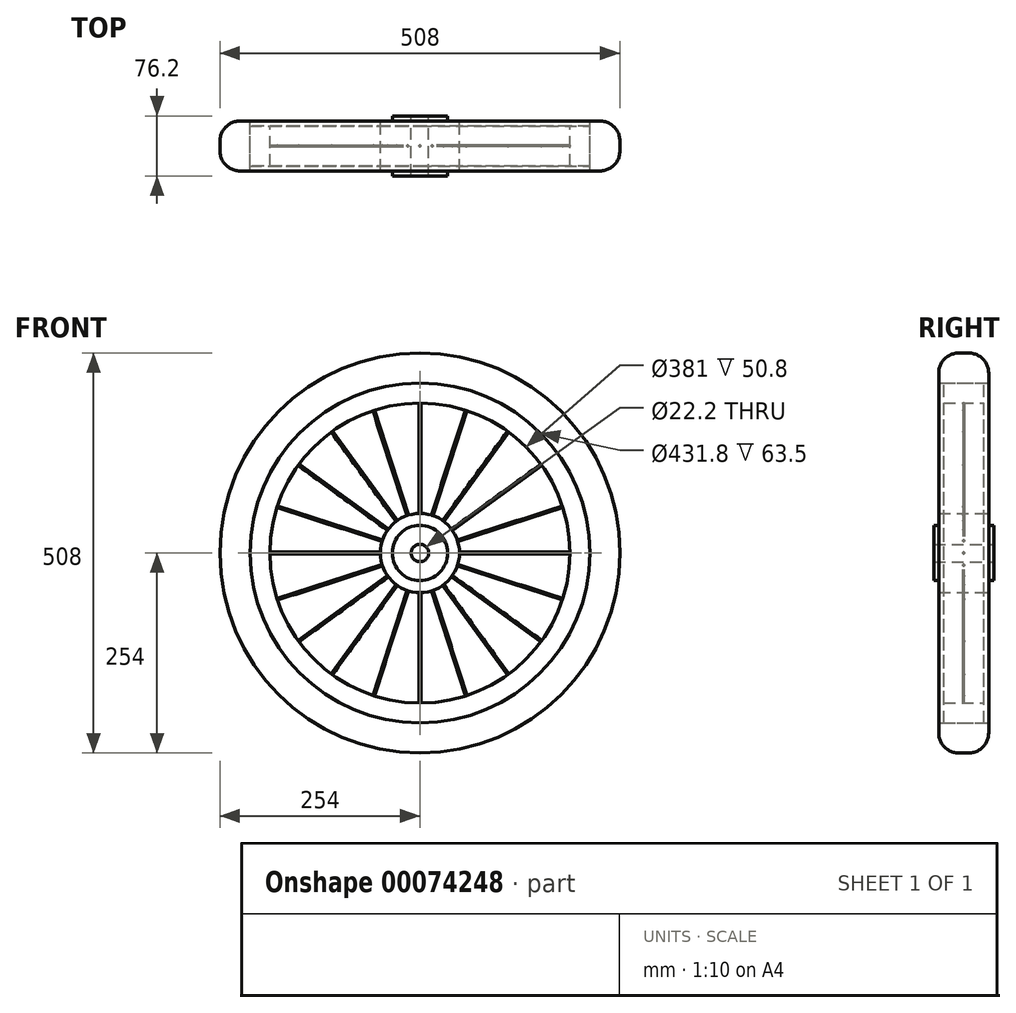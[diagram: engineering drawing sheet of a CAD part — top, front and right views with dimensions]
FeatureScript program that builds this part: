
annotation { "Feature Type Name" : "Feature", "Feature Type Description" : "" }
export const myFeature = defineFeature(function(context is Context, id is Id, definition is map)
    precondition{}
    {
        {
            var Q0;
            Q0=qCreatedBy(makeId("Front.planeOp"),FACE);
            var sketch = newSketch(context, id + "F0", { "sketchPlane" : qUnion([Q0])});
            skCircle(sketch, "E0", {"center": v(0, 0) * mm, "radius": 11.1 * mm});
            skCircle(sketch, "E1", {"center": v(0, 0) * mm, "radius": 35.13 * mm});
            skCircle(sketch, "E2", {"center": v(0, 0) * mm, "radius": 50.24 * mm});
            skCircle(sketch, "E3", {"center": v(0, 0) * mm, "radius": 190.5 * mm});
            skCircle(sketch, "E4", {"center": v(0, 0) * mm, "radius": 254 * mm});
            skLineSegment(sketch, "E5", {"start": v(-50.24, 0) * mm, "end": v(-190.5, 0) * mm});
            skCircle(sketch, "E6", {"center": v(0, 0) * mm, "radius": 215.9 * mm});
            skSolve(sketch);
        }
        {
            var Q0;
            Q0=makeQuery(id+"F0.imprint","IMPRINT",FACE,{"disambiguationData":[TD([[makeQuery(id+"F0.imprint","IMPRINT",EDGE,{"derivedFrom":sQuery(id+"F0.wireOp",EDGE,"E0")}),-1.0]])]});
            extrude(context, id + "F1", {"entities" : qUnion([Q0]), "endBound" : BoundingType.SYMMETRIC, "depth" : 76.2 * mm});
        }
        {
            var Q0;
            Q0=makeQuery(id+"F0.imprint","IMPRINT",FACE,{"disambiguationData":[TD([[makeQuery(id+"F0.imprint","IMPRINT",EDGE,{"derivedFrom":sQuery(id+"F0.wireOp",EDGE,"E1")}),-1.0]])]});
            extrude(context, id + "F2", {"entities" : qUnion([Q0]), "operationType" : NewBodyOperationType.ADD, "endBound" : BoundingType.SYMMETRIC, "depth" : 63.5 * mm});
        }
        {
            var Q0;
            Q0=makeQuery(id+"F0.imprint","IMPRINT",FACE,{"disambiguationData":[TD([[makeQuery(id+"F0.imprint","IMPRINT",EDGE,{"derivedFrom":sQuery(id+"F0.wireOp",EDGE,"E3")}),-1.0]])]});
            extrude(context, id + "F3", {"entities" : qUnion([Q0]), "endBound" : BoundingType.SYMMETRIC, "depth" : 50.8 * mm});
        }
        {
            var Q0;
            Q0=qCreatedBy(makeId("Right.planeOp"),FACE);
            var sketch = newSketch(context, id + "F4", { "sketchPlane" : qUnion([Q0])});
            skCircle(sketch, "E7", {"center": v(0, 0) * mm, "radius": 1 * mm});
            skLineSegment(sketch, "E8", {"start": v(43.84, 0) * mm, "end": v(-45.74, 0) * mm});
            skSolve(sketch);
        }
        {
            var Q0;
            Q0=qCreatedBy(makeId("Right.planeOp"),FACE);
            cPlane(context, id + "F5", {"entities" : qUnion([Q0]), "cplaneType" : CPlaneType.OFFSET, "offset" : 50.24 * mm, "oppositeDirection" : true, "width" : 152.4 * mm, "height" : 152.4 * mm});
        }
        {
            var Q0;
            Q0=qCreatedBy(id+"F5.planeOp",FACE);
            var sketch = newSketch(context, id + "F6", { "sketchPlane" : qUnion([Q0])});
            skCircle(sketch, "E9", {"center": v(0, 0) * mm, "radius": 1.06 * mm});
            skSolve(sketch);
        }
        {
            var Q0;
            Q0=makeQuery(id+"F6.imprint","IMPRINT",FACE,{"disambiguationData":[TD([[makeQuery(id+"F6.imprint","IMPRINT",EDGE,{"derivedFrom":sQuery(id+"F6.wireOp",EDGE,"E9")}),1.0]])]});
            var Q1;
            Q1=makeQuery(id+"F3.opExtrude","SWEPT_FACE",FACE,{"disambiguationData":[OSD([sQuery(id+"F0.wireOp",EDGE,"E3")])]});
            extrude(context, id + "F7", {"entities" : qUnion([Q0]), "endBound" : BoundingType.UP_TO_SURFACE, "oppositeDirection" : true, "endBoundEntityFace" : qUnion([Q1]), "depth" : 25.4 * mm});
        }
        {
            var Q0;
            Q0=makeQuery(id+"F7.opExtrude","SWEPT_BODY",BODY,{"disambiguationData":[OSD([sQuery(id+"F6.wireOp",EDGE,"E9")])]});
            var Q1;
            Q1=sQuery(id+"F4.wireOp",EDGE,"E8");
            circularPattern(context, id + "F8", {"entities" : qUnion([Q0]), "axis" : qUnion([Q1]), "angle" : 18 * degree, "instanceCount" : 20});
        }
        {
            var Q0;
            Q0=makeQuery(id+"F0.imprint","IMPRINT",FACE,{"disambiguationData":[TD([[makeQuery(id+"F0.imprint","IMPRINT",EDGE,{"derivedFrom":sQuery(id+"F0.wireOp",EDGE,"E4")}),1.0]])]});
            extrude(context, id + "F9", {"entities" : qUnion([Q0]), "endBound" : BoundingType.SYMMETRIC, "depth" : 63.5 * mm});
        }
        {
            var Q0;
            Q0=makeQuery(id+"F9.opExtrude","CAP_EDGE",EDGE,{"disambiguationData":[OSD([sQuery(id+"F0.wireOp",EDGE,"E4")])],"isStart":true});
            var Q1;
            Q1=makeQuery(id+"F9.opExtrude","CAP_EDGE",EDGE,{"disambiguationData":[OSD([sQuery(id+"F0.wireOp",EDGE,"E4")])],"isStart":false});
            fillet(context, id + "F10", {"entities" : qUnion([Q0, Q1]), "radius" : 25.4 * mm, "tangentPropagation" : true, "allowEdgeOverflow" : false});
        }
    });
